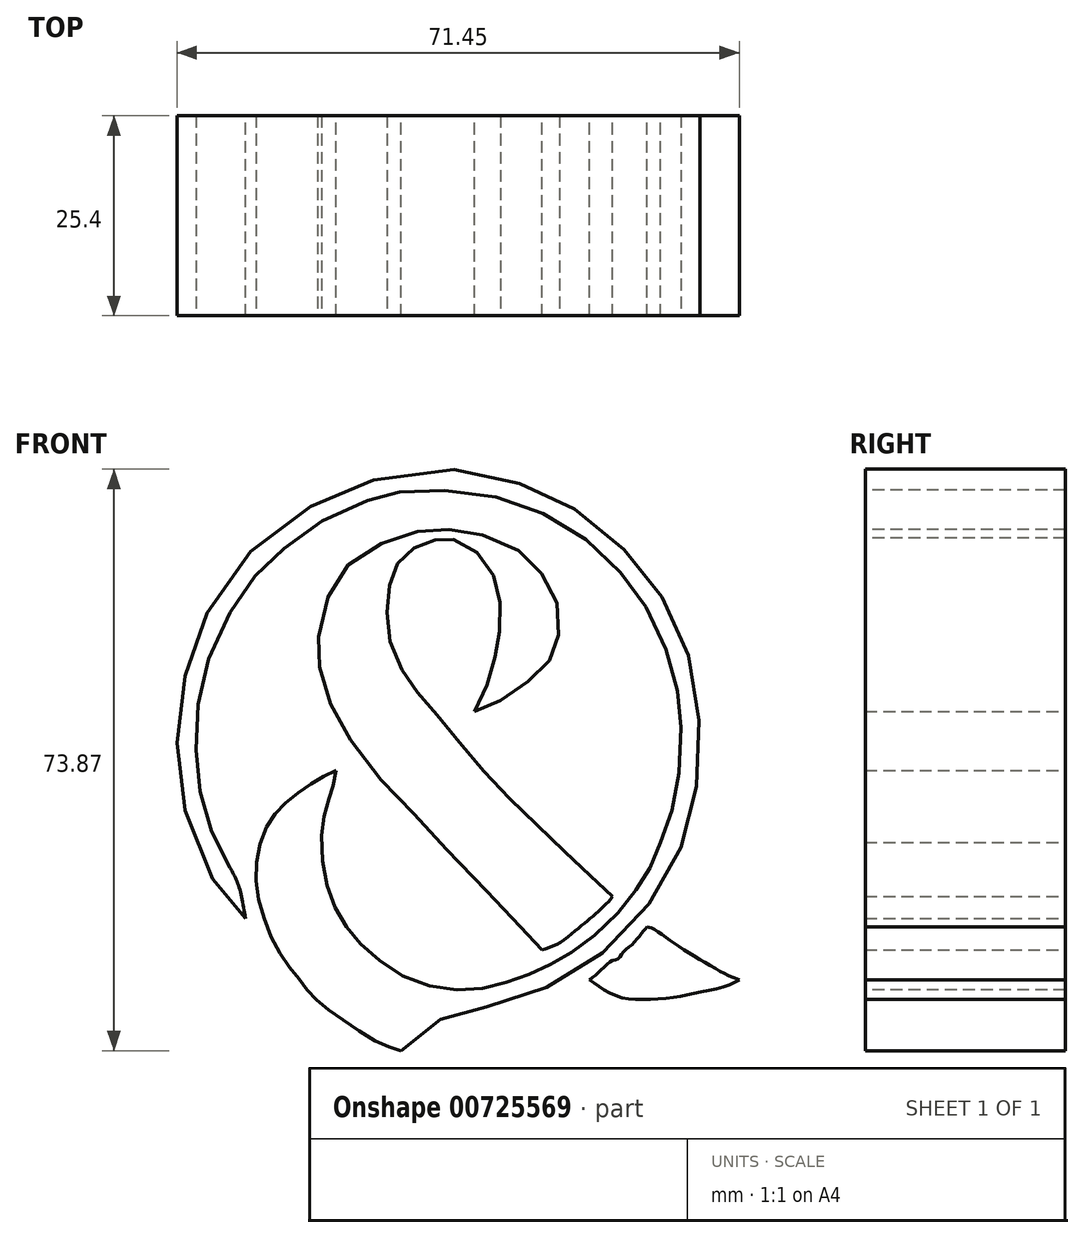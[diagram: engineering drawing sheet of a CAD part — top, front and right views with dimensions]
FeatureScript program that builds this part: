
annotation { "Feature Type Name" : "Feature", "Feature Type Description" : "" }
export const myFeature = defineFeature(function(context is Context, id is Id, definition is map)
    precondition{}
    {
        {
            var Q0;
            Q0=qCreatedBy(makeId("Front.planeOp"),FACE);
            var sketch = newSketch(context, id + "F0", { "sketchPlane" : qUnion([Q0])});
            skFitSpline(sketch, "E0", {"points": [v(2.46, 8.37) * mm, v(4.19, 12.1) * mm, v(5.2, 16.03) * mm, v(5.7, 19.21) * mm, v(5.53, 23.48) * mm, v(4.27, 26.66) * mm, v(1.35, 29.58) * mm, v(-1.3, 30.36) * mm, v(-2.7, 30.11) * mm, v(-4.95, 29.3) * mm, v(-6.96, 27.68) * mm, v(-8.12, 25.4) * mm, v(-8.61, 22.2) * mm, v(-8.5, 18.25) * mm, v(-6.9, 13.85) * mm, v(-4.88, 10.9) * mm, v(-2.04, 7.58) * mm, v(2.1, 2.49) * mm, v(6.72, -2.54) * mm, v(11.8, -7.46) * mm, v(16.66, -12.07) * mm, v(19.95, -15.14) * mm], "startDerivative": vector(37.44, 87.37) * mm, "endDerivative": vector(60.37, -53.8) * mm});
            skFitSpline(sketch, "E1", {"points": [v(19.95, -15.14) * mm, v(18.85, -16.4) * mm, v(17.37, -17.75) * mm, v(15.71, -19.11) * mm, v(13.28, -21) * mm, v(10.98, -21.95) * mm], "startDerivative": vector(-4.76, -8.67) * mm, "endDerivative": vector(-11.03, -3.51) * mm});
            skFitSpline(sketch, "E2", {"points": [v(10.98, -21.95) * mm, v(9.3, -20.17) * mm, v(5.41, -16.03) * mm, v(-1.32, -8.95) * mm, v(-5.88, -4) * mm, v(-10.6, 1.03) * mm, v(-14.55, 6.8) * mm, v(-16.33, 10.6) * mm, v(-17.38, 14.78) * mm, v(-17.46, 17.16) * mm, v(-16.57, 21.88) * mm, v(-14.43, 25.96) * mm, v(-11.61, 28.58) * mm, v(-6.49, 30.75) * mm, v(-3.7, 31.4) * mm, v(-0.6, 31.44) * mm, v(2.62, 31) * mm, v(7.1, 29.3) * mm, v(9.76, 27.37) * mm, v(11.7, 24.75) * mm, v(13.03, 21.72) * mm, v(13.15, 18.5) * mm, v(12.67, 16.32) * mm, v(11.62, 14.38) * mm, v(9.68, 12.53) * mm, v(7.02, 10.5) * mm, v(4.28, 8.98) * mm, v(2.46, 8.37) * mm], "startDerivative": vector(-52.55, 56.07) * mm, "endDerivative": vector(-68.4, -5.17) * mm});
            skFitSpline(sketch, "E3", {"points": [v(-15.18, 0.85) * mm, v(-15.4, -0.74) * mm, v(-15.85, -1.87) * mm, v(-16.12, -2.9) * mm, v(-16.74, -5.1) * mm, v(-17, -7.46) * mm, v(-16.75, -11.5) * mm, v(-15.9, -15.04) * mm, v(-14.45, -18.03) * mm, v(-12.72, -20.49) * mm, v(-9.97, -23.03) * mm, v(-5.98, -25.57) * mm, v(-1.02, -26.9) * mm, v(3.13, -26.9) * mm, v(6.72, -25.97) * mm, v(10.23, -24.72) * mm, v(13.3, -23.1) * mm, v(16.96, -20.69) * mm, v(21.52, -16.21) * mm, v(24.18, -12.42) * mm, v(26.08, -8.3) * mm], "startDerivative": vector(-2.8, -46.76) * mm, "endDerivative": vector(16.9, 82.36) * mm});
            skFitSpline(sketch, "E4", {"points": [v(26.08, -8.3) * mm, v(27.25, -5) * mm, v(28.13, -1.61) * mm, v(28.66, 4.23) * mm, v(28.54, 9.07) * mm, v(27.81, 12.74) * mm, v(25.6, 19.11) * mm, v(22.7, 23.8) * mm, v(18.82, 28.3) * mm, v(12.93, 32.54) * mm, v(6.28, 35.29) * mm, v(-1.55, 36.45) * mm, v(-7.31, 36.21) * mm, v(-10.01, 35.57) * mm, v(-16.05, 33.04) * mm, v(-21.51, 29.2) * mm, v(-24.97, 26.04) * mm, v(-28.18, 21.63) * mm, v(-31.4, 14.87) * mm, v(-32.74, 8.59) * mm, v(-32.88, 2.69) * mm, v(-32.3, -2.3) * mm, v(-30.87, -7.2) * mm, v(-28.61, -11.5) * mm], "startDerivative": vector(35.2, 96.82) * mm, "endDerivative": vector(59.42, -102.63) * mm});
            skFitSpline(sketch, "E5", {"points": [v(-28.61, -11.5) * mm, v(-27.56, -13.71) * mm, v(-26.65, -17.93) * mm], "startDerivative": vector(2.64, -4.65) * mm, "endDerivative": vector(1.35, -8.04) * mm});
            skFitSpline(sketch, "E6", {"points": [v(-26.65, -17.93) * mm, v(-29.19, -15.49) * mm, v(-31.2, -12.18) * mm, v(-34.08, -5.18) * mm, v(-35.28, 1.87) * mm, v(-35.28, 6.62) * mm, v(-34.27, 13.24) * mm, v(-32.5, 18.8) * mm, v(-29.24, 24.8) * mm, v(-23.67, 30.8) * mm, v(-17.82, 34.72) * mm, v(-12.79, 37.03) * mm, v(-3.2, 39.04) * mm, v(2.9, 38.7) * mm, v(8.8, 37.12) * mm, v(12.97, 35.3) * mm, v(17.86, 32.18) * mm, v(21.7, 28.68) * mm, v(24.77, 25.08) * mm, v(27.64, 20.38) * mm, v(29.7, 15.25) * mm, v(30.76, 9.74) * mm, v(31.05, 3.31) * mm, v(30.52, -2.06) * mm, v(29.3, -7.2) * mm, v(26.97, -12.32) * mm, v(23.9, -16.98) * mm, v(19.78, -21.44) * mm, v(14.52, -25.18) * mm, v(9.8, -27.48) * mm, v(4.52, -29.1) * mm, v(1.25, -29.53) * mm, v(-1.57, -30.62) * mm, v(-4.35, -32.2) * mm, v(-6.9, -34.74) * mm], "startDerivative": vector(-115.6, 99.84) * mm, "endDerivative": vector(-102.56, -116.35) * mm});
            skFitSpline(sketch, "E7", {"points": [v(-6.9, -34.74) * mm, v(-9.72, -33.73) * mm, v(-14.52, -30.66) * mm, v(-17.95, -28) * mm, v(-19.84, -25.66) * mm, v(-22.3, -22.36) * mm, v(-24.68, -16.71) * mm, v(-25.28, -11.06) * mm, v(-23.8, -5.94) * mm, v(-21.25, -3) * mm, v(-18.03, -0.62) * mm, v(-15.18, 0.85) * mm], "startDerivative": vector(-35.04, 9.62) * mm, "endDerivative": vector(36, 16.8) * mm});
            skFitSpline(sketch, "E8", {"points": [v(17.05, -25.72) * mm, v(18.36, -24.64) * mm, v(19.78, -23.4) * mm, v(20.67, -23.03) * mm, v(21.4, -22.17) * mm, v(22.68, -21.04) * mm, v(23.71, -19.75) * mm, v(24.36, -19.03) * mm], "startDerivative": vector(8.3, 6.24) * mm, "endDerivative": vector(5.32, 5.44) * mm});
            skFitSpline(sketch, "E9", {"points": [v(17.05, -25.72) * mm, v(18.75, -26.92) * mm, v(21.12, -28) * mm, v(24.2, -28.21) * mm, v(27.79, -27.95) * mm, v(30.76, -27.35) * mm, v(34.14, -26.63) * mm, v(36.08, -25.72) * mm], "startDerivative": vector(13.2, -9.9) * mm, "endDerivative": vector(14.1, 7.99) * mm});
            skFitSpline(sketch, "E10", {"points": [v(36.08, -25.72) * mm, v(35.37, -25.48) * mm, v(34.2, -24.95) * mm, v(31.38, -23.34) * mm, v(28.3, -21.45) * mm, v(26.1, -19.9) * mm, v(24.84, -19.12) * mm, v(24.36, -19.03) * mm], "startDerivative": vector(-7.4, 2.36) * mm, "endDerivative": vector(-5.77, 0.47) * mm});
            skSolve(sketch);
        }
        {
            var Q0;
            Q0 = qSketchRegion(id + "F0", true);
            extrude(context, id + "F1", {"entities" : qUnion([Q0]), "depth" : 25.4 * mm, "offsetDistance" : 25.4 * mm});
        }
    });
